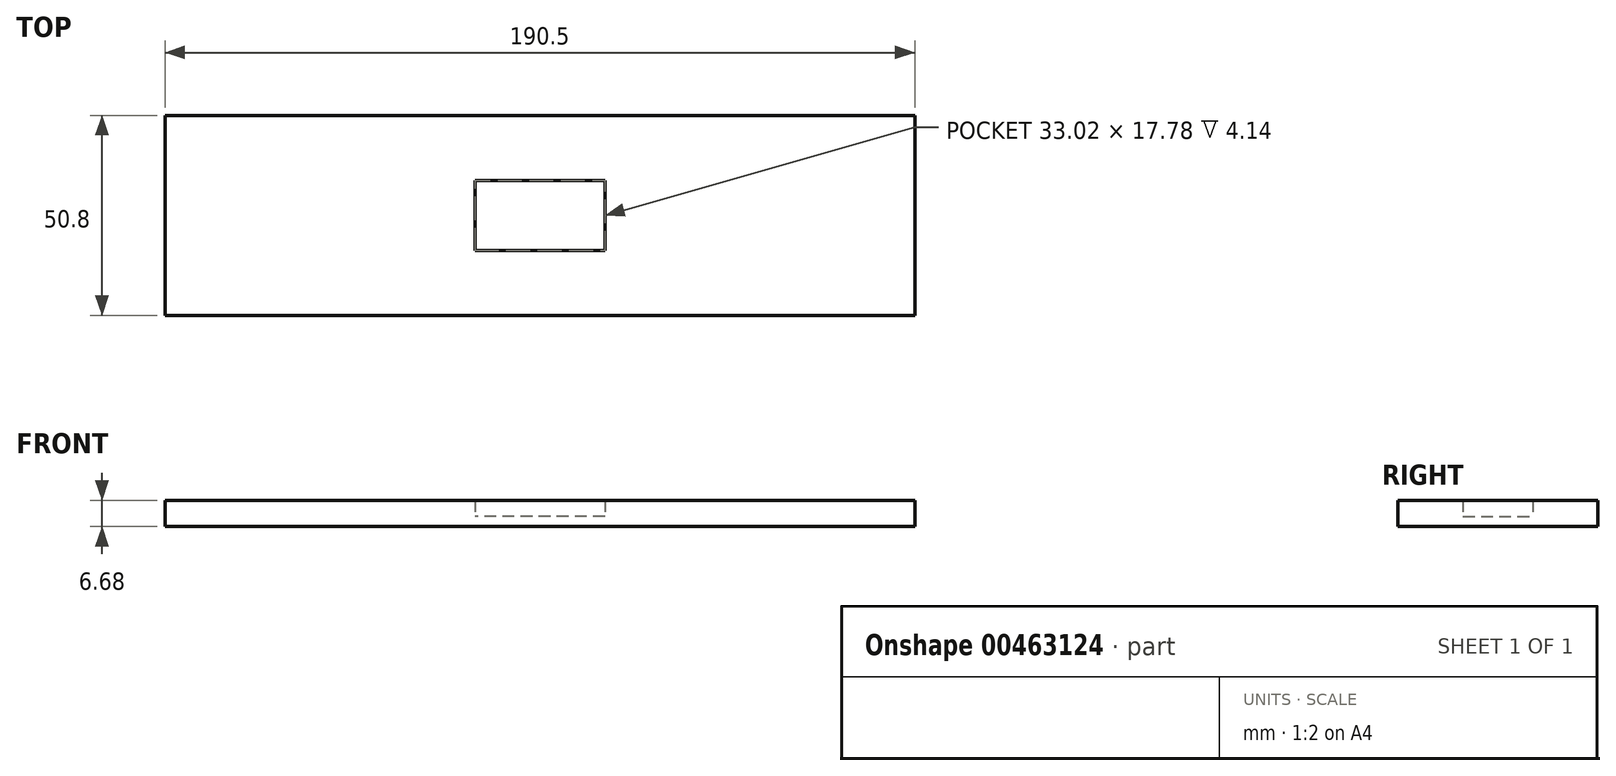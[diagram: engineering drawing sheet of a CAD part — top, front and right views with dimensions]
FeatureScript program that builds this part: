
annotation { "Feature Type Name" : "Feature", "Feature Type Description" : "" }
export const myFeature = defineFeature(function(context is Context, id is Id, definition is map)
    precondition{}
    {
        {
            var Q0;
            Q0=qCreatedBy(makeId("Top.planeOp"),FACE);
            var sketch = newSketch(context, id + "F0", { "sketchPlane" : qUnion([Q0])});
            skLineSegment(sketch, "E0.bottom", {"start": v(95.25, -25.4) * mm, "end": v(-95.25, -25.4) * mm});
            skLineSegment(sketch, "E0.top", {"start": v(95.25, 25.4) * mm, "end": v(-95.25, 25.4) * mm});
            skLineSegment(sketch, "E0.left", {"start": v(95.25, -25.4) * mm, "end": v(95.25, 25.4) * mm});
            skLineSegment(sketch, "E0.right", {"start": v(-95.25, -25.4) * mm, "end": v(-95.25, 25.4) * mm});
            skPoint(sketch, "E0.middle", {"position": v(0, 0) * mm});
            skLineSegment(sketch, "E1.bottom", {"start": v(22.23, -22.22) * mm, "end": v(-22.22, -22.23) * mm});
            skLineSegment(sketch, "E1.top", {"start": v(22.22, 22.23) * mm, "end": v(-22.23, 22.23) * mm});
            skLineSegment(sketch, "E1.left", {"start": v(22.23, -22.22) * mm, "end": v(22.22, 22.23) * mm});
            skLineSegment(sketch, "E1.right", {"start": v(-22.22, -22.23) * mm, "end": v(-22.23, 22.23) * mm});
            skLineSegment(sketch, "E2", {"start": v(0, 0) * mm, "end": v(95.25, 0) * mm});
            skLineSegment(sketch, "E3.bottom", {"start": v(16.51, -8.9) * mm, "end": v(-16.51, -8.9) * mm});
            skLineSegment(sketch, "E3.top", {"start": v(16.51, 8.9) * mm, "end": v(-16.51, 8.9) * mm});
            skLineSegment(sketch, "E3.left", {"start": v(16.51, -8.89) * mm, "end": v(16.51, 8.9) * mm});
            skLineSegment(sketch, "E3.right", {"start": v(-16.51, -8.9) * mm, "end": v(-16.51, 8.9) * mm});
            skSolve(sketch);
        }
        {
            var Q0;
            {var subQ7=sQuery(id+"F0.wireOp",EDGE,"E0.bottom");Q0=makeQuery(id+"F0.imprint","IMPRINT",FACE,{"disambiguationData":[TD([[makeQuery(id+"F0.imprint","IMPRINT",EDGE,{"derivedFrom":subQ7}),-1.0]])]});}
            extrude(context, id + "F1", {"entities" : qUnion([Q0]), "depth" : 6.68 * mm, "offsetDistance" : 25.4 * mm});
        }
        {
            var Q0;
            {var subQ3=sQuery(id+"F0.wireOp",EDGE,"E3.bottom");Q0=makeQuery(id+"F0.imprint","IMPRINT",FACE,{"disambiguationData":[TD([[makeQuery(id+"F0.imprint","IMPRINT",EDGE,{"derivedFrom":subQ3}),-1.0]])]});}
            extrude(context, id + "F2", {"entities" : qUnion([Q0]), "depth" : 2.54 * mm, "offsetDistance" : 25.4 * mm});
        }
        {
            var Q0;
            {var subQ3=sQuery(id+"F0.wireOp",EDGE,"E1.bottom");Q0=makeQuery(id+"F0.imprint","IMPRINT",FACE,{"disambiguationData":[TD([[makeQuery(id+"F0.imprint","IMPRINT",EDGE,{"derivedFrom":subQ3}),-1.0]])]});}
            var Q1;
            {var subQ3=sQuery(id+"F0.wireOp",EDGE,"E0.bottom");Q1=makeQuery(id+"F0.imprint","IMPRINT",FACE,{"disambiguationData":[TD([[makeQuery(id+"F0.imprint","IMPRINT",EDGE,{"derivedFrom":subQ3}),-1.0]])]});}
            extrude(context, id + "F3", {"entities" : qUnion([Q0, Q1]), "operationType" : NewBodyOperationType.ADD, "depth" : 6.68 * mm, "offsetDistance" : 25.4 * mm});
        }
    });
